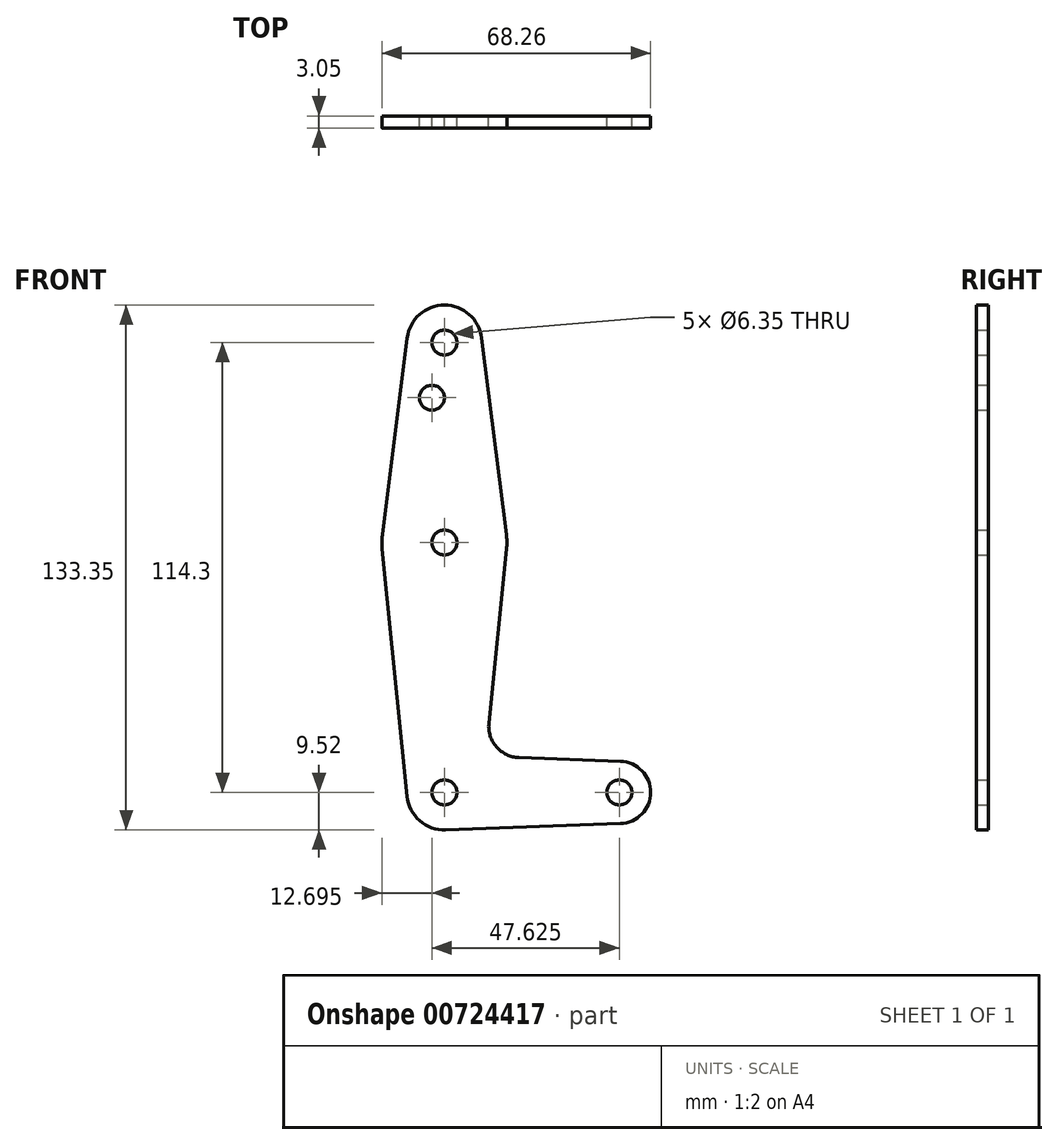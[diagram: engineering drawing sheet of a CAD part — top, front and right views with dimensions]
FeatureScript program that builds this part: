
annotation { "Feature Type Name" : "Feature", "Feature Type Description" : "" }
export const myFeature = defineFeature(function(context is Context, id is Id, definition is map)
    precondition{}
    {
        {
            var Q0;
            Q0=qCreatedBy(makeId("Front.planeOp"),FACE);
            var sketch = newSketch(context, id + "F0", { "sketchPlane" : qUnion([Q0])});
            skLineSegment(sketch, "E0", {"start": v(0, 0) * mm, "end": v(0, 114.3) * mm, "construction": true});
            skLineSegment(sketch, "E1", {"start": v(0, 0) * mm, "end": v(44.45, 0) * mm, "construction": true});
            skCircle(sketch, "E2", {"center": v(0, 0) * mm, "radius": 9.53 * mm});
            skCircle(sketch, "E3", {"center": v(0, 114.3) * mm, "radius": 9.53 * mm});
            skCircle(sketch, "E4", {"center": v(44.45, 0) * mm, "radius": 7.94 * mm});
            skCircle(sketch, "E5", {"center": v(0, 63.5) * mm, "radius": 15.88 * mm});
            skLineSegment(sketch, "E6", {"start": v(-15.8, 61.91) * mm, "end": v(-9.48, -0.95) * mm});
            skLineSegment(sketch, "E7", {"start": v(15.8, 61.9) * mm, "end": v(11.3, 17.6) * mm});
            skLineSegment(sketch, "E8", {"start": v(-9.45, 115.5) * mm, "end": v(-15.75, 65.48) * mm});
            skLineSegment(sketch, "E9", {"start": v(9.45, 115.5) * mm, "end": v(15.75, 65.48) * mm});
            skLineSegment(sketch, "E10", {"start": v(0.34, -9.52) * mm, "end": v(44.73, -7.93) * mm});
            skLineSegment(sketch, "E11", {"start": v(18.93, 8.85) * mm, "end": v(44.73, 7.93) * mm});
            skCircle(sketch, "E12", {"center": v(0, 114.3) * mm, "radius": 3.18 * mm});
            skCircle(sketch, "E13", {"center": v(0, 63.5) * mm, "radius": 3.18 * mm});
            skCircle(sketch, "E14", {"center": v(0, 0) * mm, "radius": 3.18 * mm});
            skCircle(sketch, "E15", {"center": v(44.45, 0) * mm, "radius": 3.18 * mm});
            skCircle(sketch, "E16", {"center": v(-3.18, 100.27) * mm, "radius": 3.18 * mm});
            skArc(sketch, "E17.filletArc", {"start": v(11.3, 17.6) * mm, "mid": v(13.22, 11.57) * mm, "end": v(18.93, 8.85) * mm});
            skSolve(sketch);
        }
        {
            var Q0;
            Q0 = qSketchRegion(id + "F0", true);
            extrude(context, id + "F1", {"entities" : qUnion([Q0]), "depth" : 3.05 * mm, "offsetDistance" : 25.4 * mm});
        }
    });
